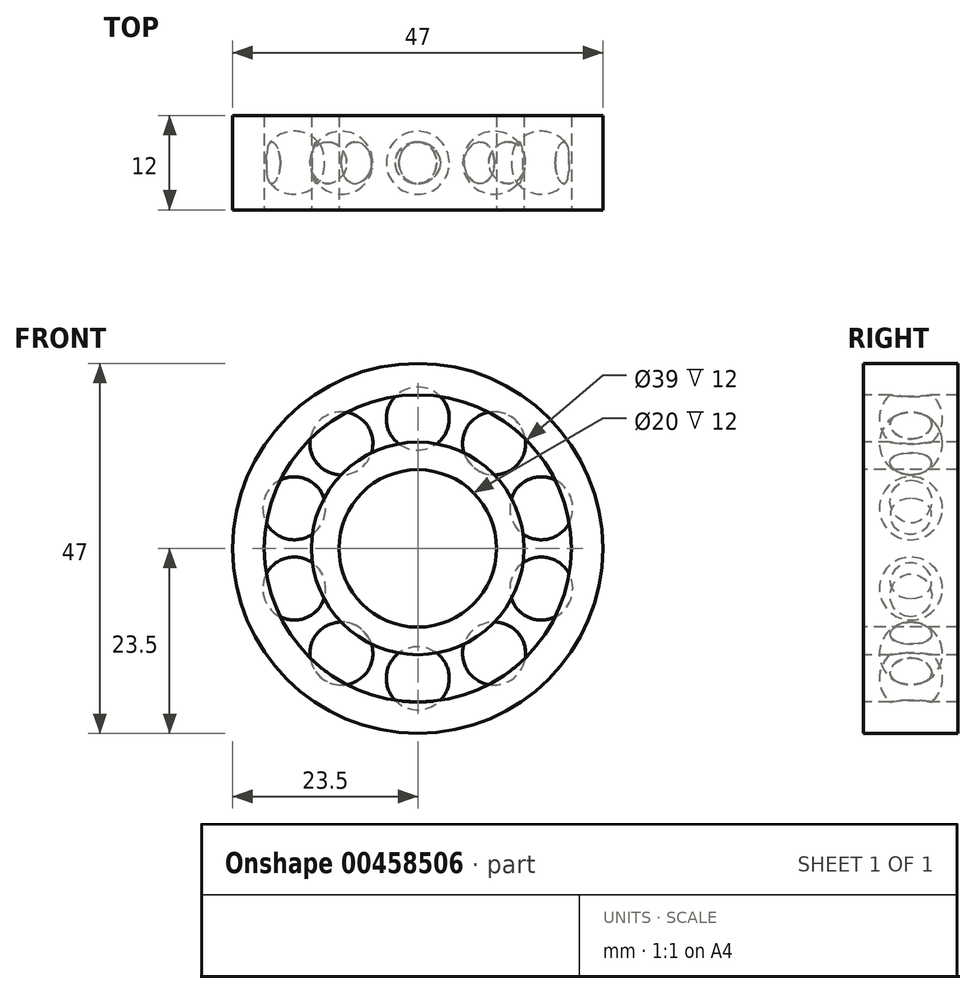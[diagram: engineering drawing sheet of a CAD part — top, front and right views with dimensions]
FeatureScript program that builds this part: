
annotation { "Feature Type Name" : "Feature", "Feature Type Description" : "" }
export const myFeature = defineFeature(function(context is Context, id is Id, definition is map)
    precondition{}
    {
        {
            var Q0;
            Q0=qCreatedBy(makeId("Front.planeOp"),FACE);
            var sketch = newSketch(context, id + "F0", { "sketchPlane" : qUnion([Q0])});
            skCircle(sketch, "E0", {"center": v(0, 0) * mm, "radius": 10 * mm});
            skCircle(sketch, "E1", {"center": v(0, 0) * mm, "radius": 19.5 * mm});
            skCircle(sketch, "E2", {"center": v(0, 0) * mm, "radius": 23.5 * mm});
            skCircle(sketch, "E3", {"center": v(0, 0) * mm, "radius": 13.5 * mm});
            skSolve(sketch);
        }
        {
            var Q0;
            Q0=qCreatedBy(makeId("Front.planeOp"),FACE);
            cPlane(context, id + "F1", {"entities" : qUnion([Q0]), "cplaneType" : CPlaneType.OFFSET, "offset" : 6 * mm, "oppositeDirection" : true, "width" : 150 * mm, "height" : 150 * mm});
        }
        {
            var Q0;
            Q0=makeQuery(id+"F0.imprint","IMPRINT",FACE,{"disambiguationData":[TD([[makeQuery(id+"F0.imprint","IMPRINT",EDGE,{"derivedFrom":sQuery(id+"F0.wireOp",EDGE,"E1")}),-1.0]])]});
            extrude(context, id + "F2", {"entities" : qUnion([Q0]), "oppositeDirection" : true, "depth" : 12 * mm});
        }
        {
            var Q0;
            Q0=makeQuery(id+"F0.imprint","IMPRINT",FACE,{"disambiguationData":[TD([[makeQuery(id+"F0.imprint","IMPRINT",EDGE,{"derivedFrom":sQuery(id+"F0.wireOp",EDGE,"E0")}),-1.0]])]});
            extrude(context, id + "F3", {"entities" : qUnion([Q0]), "operationType" : NewBodyOperationType.ADD, "oppositeDirection" : true, "depth" : 12 * mm});
        }
        {
            var Q0;
            Q0=qCreatedBy(id+"F1.planeOp",FACE);
            var sketch = newSketch(context, id + "F4", { "sketchPlane" : qUnion([Q0])});
            skArc(sketch, "E4", {"start": v(0, 12.5) * mm, "mid": v(4, 16.5) * mm, "end": v(0, 20.5) * mm});
            skLineSegment(sketch, "E5", {"start": v(0, 20.5) * mm, "end": v(0, 12.5) * mm});
            skPoint(sketch, "E6.orphan", {"position": v(0, 24.94) * mm});
            skSolve(sketch);
        }
        {
            var Q0;
            Q0 = qSketchRegion(id + "F4", true);
            var Q1;
            Q1=sQuery(id+"F4.wireOp",EDGE,"E5");
            revolve(context, id + "F5", {"entities" : qUnion([Q0]), "axis" : qUnion([Q1]), "revolveType" : RevolveType.FULL});
        }
        {
            var Q0;
            Q0=makeQuery(id+"F5.opRevolve","SWEPT_BODY",BODY,{"disambiguationData":[OSD([sQuery(id+"F4.wireOp",EDGE,"E4"),sQuery(id+"F4.wireOp",EDGE,"E5")])]});
            var Q1;
            Q1=sQuery(id+"F0.wireOp",EDGE,"E0");
            circularPattern(context, id + "F6", {"operationType" : NewBodyOperationType.ADD, "entities" : qUnion([Q0]), "axis" : qUnion([Q1]), "angle" : 360 * degree, "instanceCount" : 10, "equalSpace" : true});
        }
    });
